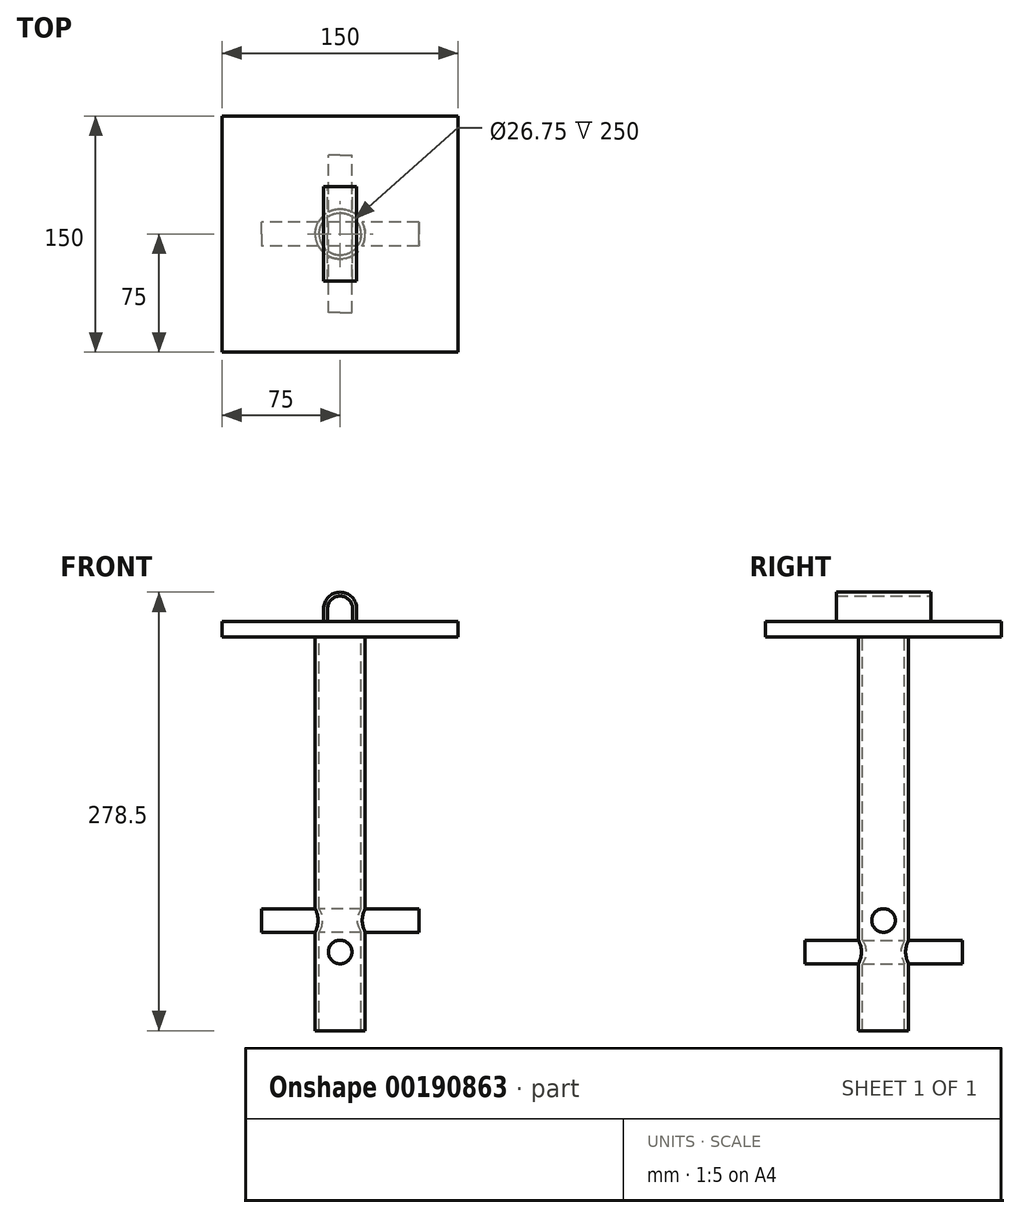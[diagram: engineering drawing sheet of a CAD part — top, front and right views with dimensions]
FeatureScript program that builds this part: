
annotation { "Feature Type Name" : "Feature", "Feature Type Description" : "" }
export const myFeature = defineFeature(function(context is Context, id is Id, definition is map)
    precondition{}
    {
        {
            var Q0;
            Q0=qCreatedBy(makeId("Top.planeOp"),FACE);
            var sketch = newSketch(context, id + "F0", { "sketchPlane" : qUnion([Q0])});
            skLineSegment(sketch, "E0.bottom", {"start": v(-75, 75) * mm, "end": v(75, 75) * mm});
            skLineSegment(sketch, "E0.top", {"start": v(-75, -75) * mm, "end": v(75, -75) * mm});
            skLineSegment(sketch, "E0.left", {"start": v(-75, 75) * mm, "end": v(-75, -75) * mm});
            skLineSegment(sketch, "E0.right", {"start": v(75, 75) * mm, "end": v(75, -75) * mm});
            skPoint(sketch, "E0.middle", {"position": v(0, 0) * mm});
            skSolve(sketch);
        }
        {
            var Q0;
            Q0=makeQuery(id+"F0.imprint","IMPRINT",FACE,{"disambiguationData":[TD([[makeQuery(id+"F0.imprint","IMPRINT",EDGE,{"derivedFrom":sQuery(id+"F0.wireOp",EDGE,"E0.bottom")}),-1.0]])]});
            extrude(context, id + "F1", {"entities" : qUnion([Q0]), "oppositeDirection" : true, "depth" : 10 * mm});
        }
        {
            var Q0;
            Q0=makeQuery(id+"F1.opExtrude","CAP_FACE",FACE,{"disambiguationData":[OSD([sQuery(id+"F0.wireOp",EDGE,"E0.bottom"),sQuery(id+"F0.wireOp",EDGE,"E0.top"),sQuery(id+"F0.wireOp",EDGE,"E0.left"),sQuery(id+"F0.wireOp",EDGE,"E0.right")])],"isStart":false});
            var sketch = newSketch(context, id + "F2", { "sketchPlane" : qUnion([Q0])});
            skCircle(sketch, "E1", {"center": v(0, 0) * mm, "radius": 15.88 * mm});
            skCircle(sketch, "E2", {"center": v(0, 0) * mm, "radius": 13.38 * mm});
            skSolve(sketch);
        }
        {
            var Q0;
            Q0=makeQuery(id+"F2.imprint","IMPRINT",FACE,{"disambiguationData":[TD([[makeQuery(id+"F2.imprint","IMPRINT",EDGE,{"derivedFrom":sQuery(id+"F2.wireOp",EDGE,"E1")}),1.0]])]});
            extrude(context, id + "F3", {"entities" : qUnion([Q0]), "operationType" : NewBodyOperationType.ADD, "depth" : 250 * mm});
        }
        {
            var Q0;
            Q0=qCreatedBy(makeId("Front.planeOp"),FACE);
            var sketch = newSketch(context, id + "F4", { "sketchPlane" : qUnion([Q0])});
            skCircle(sketch, "E3", {"center": v(0, -210) * mm, "radius": 7.5 * mm});
            skSolve(sketch);
        }
        {
            var Q0;
            Q0=makeQuery(id+"F4.imprint","IMPRINT",FACE,{"disambiguationData":[TD([[makeQuery(id+"F4.imprint","IMPRINT",EDGE,{"derivedFrom":sQuery(id+"F4.wireOp",EDGE,"E3")}),1.0]])]});
            extrude(context, id + "F5", {"entities" : qUnion([Q0]), "operationType" : NewBodyOperationType.ADD, "endBound" : BoundingType.SYMMETRIC, "depth" : 100 * mm});
        }
        {
            var Q0;
            Q0=qCreatedBy(makeId("Right.planeOp"),FACE);
            var sketch = newSketch(context, id + "F6", { "sketchPlane" : qUnion([Q0])});
            skCircle(sketch, "E4", {"center": v(0, -190) * mm, "radius": 7.5 * mm});
            skSolve(sketch);
        }
        {
            var Q0;
            Q0 = qSketchRegion(id + "F6", true);
            extrude(context, id + "F7", {"entities" : qUnion([Q0]), "operationType" : NewBodyOperationType.ADD, "endBound" : BoundingType.SYMMETRIC, "depth" : 100 * mm});
        }
        {
            var Q0;
            Q0=qCreatedBy(makeId("Front.planeOp"),FACE);
            var sketch = newSketch(context, id + "F8", { "sketchPlane" : qUnion([Q0])});
            skLineSegment(sketch, "E5", {"start": v(-10.5, 0) * mm, "end": v(-10.5, 8) * mm});
            skLineSegment(sketch, "E6", {"start": v(-10.5, 0) * mm, "end": v(-8, 0) * mm});
            skLineSegment(sketch, "E7", {"start": v(-8, 0) * mm, "end": v(-8, 8) * mm});
            skArc(sketch, "E8", {"start": v(0, 16) * mm, "mid": v(-5.66, 13.66) * mm, "end": v(-8, 8) * mm});
            skArc(sketch, "E9.0", {"start": v(0, 18.5) * mm, "mid": v(-7.42, 15.42) * mm, "end": v(-10.5, 8) * mm});
            skArc(sketch, "E10.MirrorCS", {"start": v(0, 16) * mm, "mid": v(5.66, 13.66) * mm, "end": v(8, 8) * mm});
            skArc(sketch, "E11.MirrorCS", {"start": v(0, 18.5) * mm, "mid": v(7.42, 15.42) * mm, "end": v(10.5, 8) * mm});
            skLineSegment(sketch, "E12.MirrorCS", {"start": v(10.5, 0) * mm, "end": v(10.5, 8) * mm});
            skLineSegment(sketch, "E13.MirrorCS", {"start": v(8, 0) * mm, "end": v(8, 8) * mm});
            skLineSegment(sketch, "E14.MirrorCS", {"start": v(10.5, 0) * mm, "end": v(8, 0) * mm});
            skSolve(sketch);
        }
        {
            var Q0;
            Q0=makeQuery(id+"F8.imprint","IMPRINT",FACE,{"disambiguationData":[TD([[makeQuery(id+"F8.imprint","IMPRINT",EDGE,{"derivedFrom":sQuery(id+"F8.wireOp",EDGE,"BkNTylZe-JUrD-aLBX-w6gX-NHBVFb0Z43Rc")}),-1.0]])]});
            var Q1;
            Q1=makeQuery(id+"F8.imprint","IMPRINT",FACE,{"disambiguationData":[TD([[makeQuery(id+"F8.imprint","IMPRINT",EDGE,{"derivedFrom":sQuery(id+"F8.wireOp",EDGE,"E5")}),-1.0]])]});
            extrude(context, id + "F9", {"entities" : qUnion([Q0, Q1]), "operationType" : NewBodyOperationType.ADD, "endBound" : BoundingType.SYMMETRIC, "depth" : 60 * mm});
        }
    });
